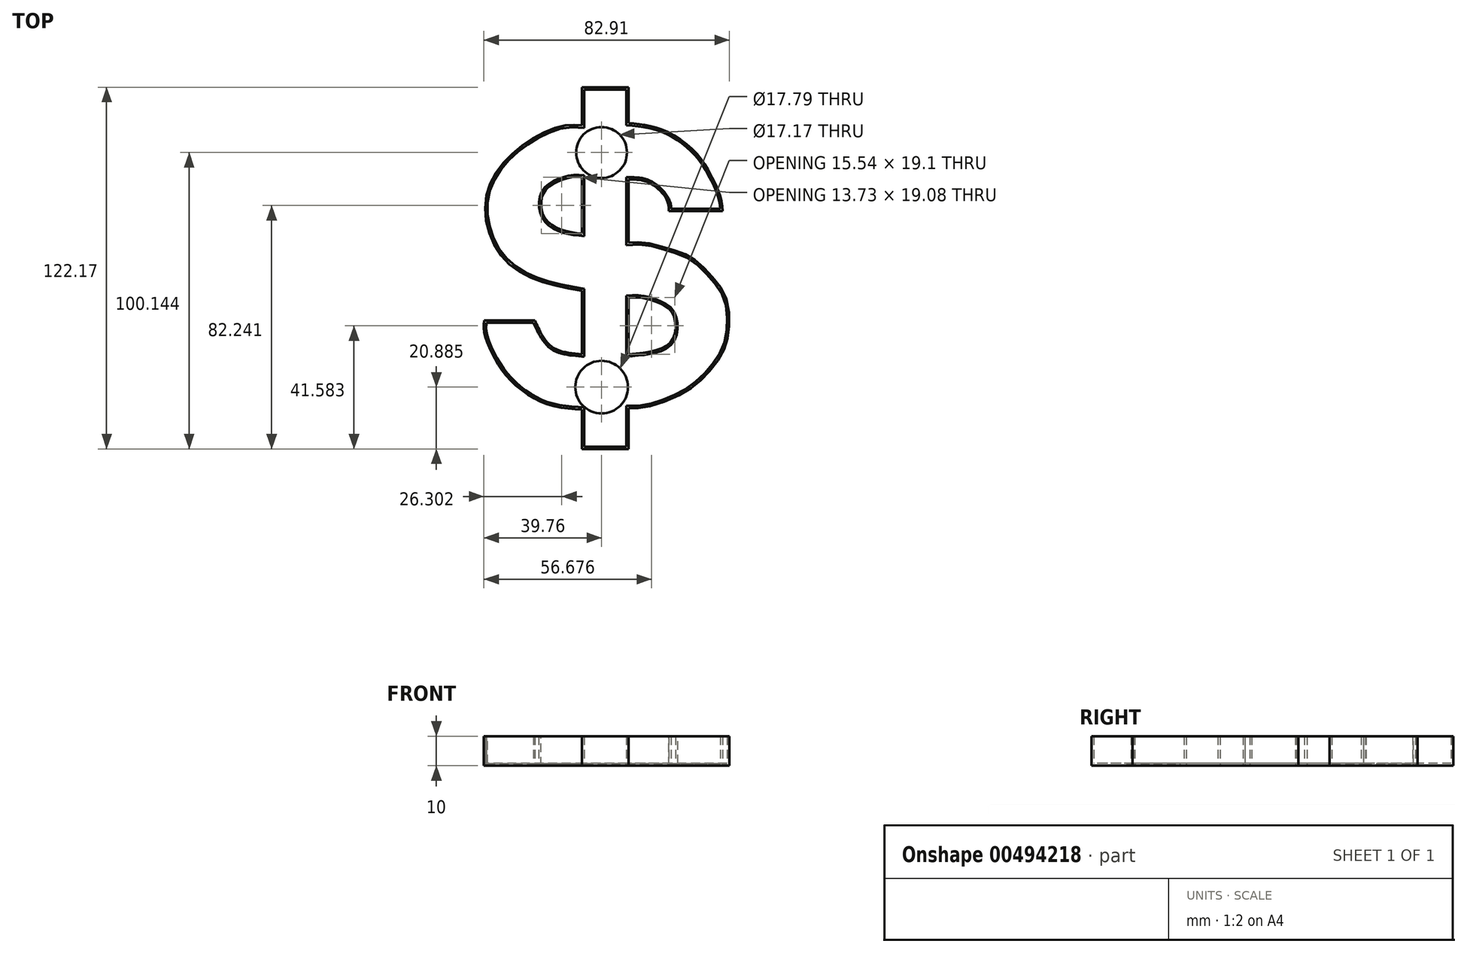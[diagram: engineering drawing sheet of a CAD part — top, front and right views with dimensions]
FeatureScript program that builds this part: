
annotation { "Feature Type Name" : "Feature", "Feature Type Description" : "" }
export const myFeature = defineFeature(function(context is Context, id is Id, definition is map)
    precondition{}
    {
        {
            var Q0;
            Q0=qCreatedBy(makeId("Top.planeOp"),FACE);
            var sketch = newSketch(context, id + "F0", { "sketchPlane" : qUnion([Q0])});
            skLineSegment(sketch, "E0", {"start": v(-6.6, 63.7) * mm, "end": v(-6.6, 50.83) * mm});
            skLineSegment(sketch, "E1", {"start": v(-6.6, 63.7) * mm, "end": v(9.14, 63.7) * mm});
            skLineSegment(sketch, "E2", {"start": v(9.14, 63.7) * mm, "end": v(9.14, 51.59) * mm});
            skLineSegment(sketch, "E3", {"start": v(9.14, 32.58) * mm, "end": v(9.14, 11.16) * mm});
            skLineSegment(sketch, "E4", {"start": v(-6.6, 33.3) * mm, "end": v(-6.6, 14.22) * mm});
            skLineSegment(sketch, "E5", {"start": v(9.14, -7.37) * mm, "end": v(9.14, -26.45) * mm});
            skLineSegment(sketch, "E6", {"start": v(-6.6, -5.03) * mm, "end": v(-6.6, -26.45) * mm});
            skLineSegment(sketch, "E7", {"start": v(9.14, -44.62) * mm, "end": v(9.14, -58.48) * mm});
            skLineSegment(sketch, "E8", {"start": v(-6.6, -45.16) * mm, "end": v(-6.6, -58.48) * mm});
            skLineSegment(sketch, "E9", {"start": v(-6.6, -58.48) * mm, "end": v(9.14, -58.48) * mm});
            skLineSegment(sketch, "E10", {"start": v(22.68, 21.87) * mm, "end": v(40.93, 21.87) * mm});
            skPoint(sketch, "E10.startSnap0", {"position": v(9.14, 21.87) * mm});
            skLineSegment(sketch, "E11", {"start": v(-39.64, -15.12) * mm, "end": v(-22.5, -15.12) * mm});
            skFitSpline(sketch, "E12", {"points": [v(-6.6, 50.83) * mm, v(-12.35, 50.83) * mm, v(-22.5, 46.83) * mm, v(-32.82, 38.53) * mm, v(-38.71, 28.02) * mm, v(-38.16, 15.12) * mm, v(-31.7, 4.42) * mm, v(-20.65, -1.84) * mm, v(-6.6, -5.03) * mm], "startDerivative": vector(-61.3, 6.08) * mm, "endDerivative": vector(103.67, -18.23) * mm});
            skFitSpline(sketch, "E13", {"points": [v(9.14, 51.59) * mm, v(15.3, 50.83) * mm, v(23.23, 48.12) * mm, v(32.26, 41.11) * mm, v(36.87, 34.1) * mm, v(40, 27.28) * mm, v(40.93, 21.87) * mm], "startDerivative": vector(40.52, -3.54) * mm, "endDerivative": vector(3.67, -37.88) * mm});
            skFitSpline(sketch, "E14", {"points": [v(22.68, 21.87) * mm, v(22.68, 23.64) * mm, v(21.02, 27.28) * mm, v(15.49, 31.7) * mm, v(9.14, 32.58) * mm], "startDerivative": vector(1.03, 10.5) * mm, "endDerivative": vector(-21.64, 0.17) * mm});
            skFitSpline(sketch, "E15", {"points": [v(-6.6, 33.3) * mm, v(-9.96, 33.3) * mm, v(-16.22, 31.16) * mm, v(-19.91, 27.28) * mm, v(-19.54, 20.28) * mm, v(-14.38, 15.85) * mm, v(-6.6, 14.22) * mm], "startDerivative": vector(-24.62, 2.27) * mm, "endDerivative": vector(42.49, -5.26) * mm});
            skFitSpline(sketch, "E16", {"points": [v(9.14, 11.16) * mm, v(14.75, 11.16) * mm, v(24.33, 8.66) * mm, v(30.79, 5.9) * mm, v(37.06, 0) * mm, v(42.22, -7.93) * mm, v(42.95, -18.44) * mm, v(40.93, -25.8) * mm, v(34.84, -33.92) * mm, v(27.47, -39.64) * mm, v(15.3, -44.25) * mm, v(9.14, -44.62) * mm], "startDerivative": vector(70.63, 5.98) * mm, "endDerivative": vector(-72.24, 2.34) * mm});
            skFitSpline(sketch, "E17", {"points": [v(9.14, -7.37) * mm, v(13.27, -7.37) * mm, v(19.54, -9.22) * mm, v(23.97, -12.72) * mm, v(24.52, -20.1) * mm, v(20.28, -24.52) * mm, v(9.14, -26.45) * mm], "startDerivative": vector(29.69, 2.28) * mm, "endDerivative": vector(-57.15, -4.67) * mm});
            skFitSpline(sketch, "E18", {"points": [v(-22.5, -15.12) * mm, v(-20.65, -18.99) * mm, v(-16.22, -24.33) * mm, v(-6.6, -26.45) * mm], "startDerivative": vector(6.11, -13.8) * mm, "endDerivative": vector(26.72, -2.09) * mm});
            skFitSpline(sketch, "E19", {"points": [v(-39.64, -15.12) * mm, v(-39.64, -18.8) * mm, v(-36.87, -26.45) * mm, v(-30.42, -35.58) * mm, v(-18.99, -43.14) * mm, v(-6.6, -45.16) * mm], "startDerivative": vector(-2.67, -27.06) * mm, "endDerivative": vector(54.28, -3.55) * mm});
            skSolve(sketch);
        }
        {
            var Q0;
            Q0=makeQuery(id+"F0.imprint","IMPRINT",FACE,{"disambiguationData":[TD([[makeQuery(id+"F0.imprint","IMPRINT",EDGE,{"derivedFrom":sQuery(id+"F0.wireOp",EDGE,"E0")}),1.0]])]});
            extrude(context, id + "F1", {"entities" : qUnion([Q0]), "depth" : 10 * mm});
        }
        {
            var Q0;
            Q0=makeQuery(id+"F1.opExtrude","CAP_FACE",FACE,{"disambiguationData":[OSD([sQuery(id+"F0.wireOp",EDGE,"E0"),sQuery(id+"F0.wireOp",EDGE,"E1"),sQuery(id+"F0.wireOp",EDGE,"E2"),sQuery(id+"F0.wireOp",EDGE,"E3"),sQuery(id+"F0.wireOp",EDGE,"E4"),sQuery(id+"F0.wireOp",EDGE,"E5"),sQuery(id+"F0.wireOp",EDGE,"E6"),sQuery(id+"F0.wireOp",EDGE,"E7"),sQuery(id+"F0.wireOp",EDGE,"E8"),sQuery(id+"F0.wireOp",EDGE,"E9"),sQuery(id+"F0.wireOp",EDGE,"E10"),sQuery(id+"F0.wireOp",EDGE,"E11"),sQuery(id+"F0.wireOp",EDGE,"E12"),sQuery(id+"F0.wireOp",EDGE,"E13"),sQuery(id+"F0.wireOp",EDGE,"E14"),sQuery(id+"F0.wireOp",EDGE,"E15"),sQuery(id+"F0.wireOp",EDGE,"E16"),sQuery(id+"F0.wireOp",EDGE,"E17"),sQuery(id+"F0.wireOp",EDGE,"E18"),sQuery(id+"F0.wireOp",EDGE,"E19")])],"isStart":false});
            shell(context, id + "F2", {"entities" : qUnion([Q0]), "thickness" : 0.76 * mm});
        }
        {
            var Q0;
            Q0=qCreatedBy(makeId("Top.planeOp"),FACE);
            var sketch = newSketch(context, id + "F3", { "sketchPlane" : qUnion([Q0])});
            skCircle(sketch, "E20", {"center": v(0, 41.66) * mm, "radius": 8.59 * mm});
            skCircle(sketch, "E21", {"center": v(0, -37.6) * mm, "radius": 8.9 * mm});
            skSolve(sketch);
        }
        {
            var Q0;
            Q0 = qSketchRegion(id + "F3", true);
            extrude(context, id + "F4", {"entities" : qUnion([Q0]), "operationType" : NewBodyOperationType.REMOVE, "depth" : 25.4 * mm});
        }
    });
